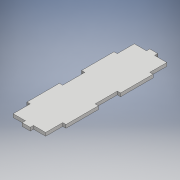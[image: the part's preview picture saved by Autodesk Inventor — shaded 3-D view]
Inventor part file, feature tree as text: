
AUTODESK INVENTOR PART (.ipt)
format: ipt  version: 2018 (Build 220112000, 112)  size: 152,064 bytes
history: native  units: mm
features: extrude x2, sketch x2, projected_geometry x1
ambient origin geometry x8: Origin, YZ Plane, XZ Plane, XY Plane, X Axis, Y Axis, Z Axis, Center Point
bodies: Body1 (feature_tree)
feature tree (5):
  extrude  "Extrusion3"  Depth=40.0mm
  extrude  "Extrusion4"  Depth=4.0mm TaperAngle=0.0deg
  sketch  "Sketch2"  dims[d15=4.0mm d16=40.0mm]
  sketch  "Sketch3"  dims[d17=4.0mm d18=4.0mm d19=0.0mm d20=40.0mm d21=40.0mm d22=149.2mm d23=10.0mm d24=4.0mm d25=149.2mm d26=74.6mm d27=4.0mm d28=0.0mm]
  projected_geometry  "Projected Loop1"
